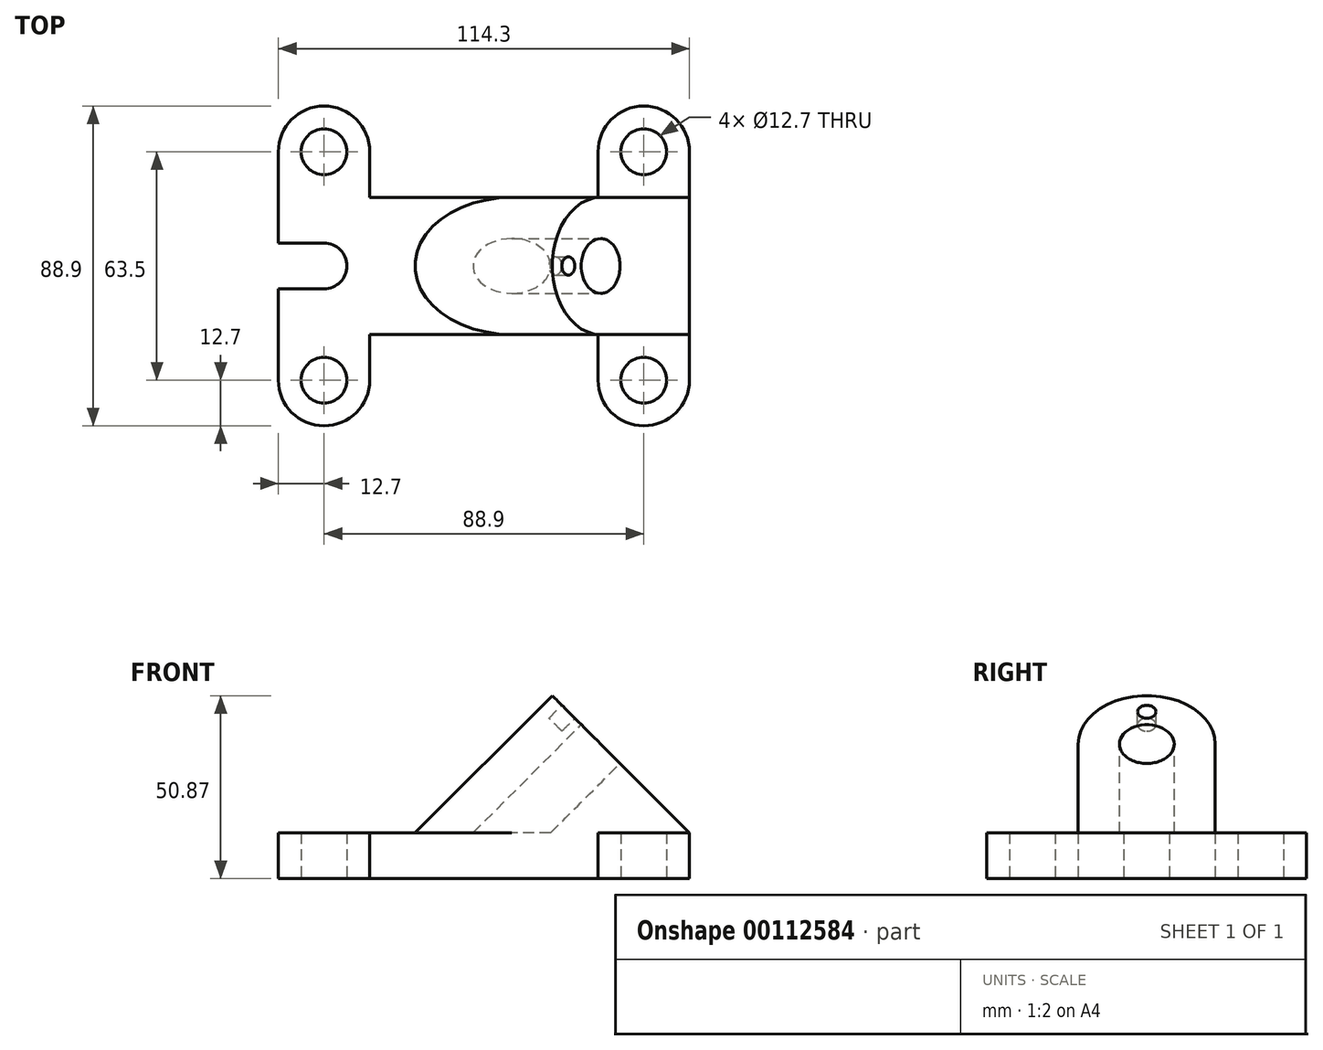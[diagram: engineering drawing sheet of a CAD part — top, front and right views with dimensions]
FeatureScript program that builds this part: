
annotation { "Feature Type Name" : "Feature", "Feature Type Description" : "" }
export const myFeature = defineFeature(function(context is Context, id is Id, definition is map)
    precondition{}
    {
        {
            var Q0;
            Q0=qCreatedBy(makeId("Top.planeOp"),FACE);
            var sketch = newSketch(context, id + "F0", { "sketchPlane" : qUnion([Q0])});
            skLineSegment(sketch, "E0", {"start": v(-14.51, 0) * mm, "end": v(127.31, 0) * mm, "construction": true});
            skLineSegment(sketch, "E1", {"start": v(0, 6.35) * mm, "end": v(0, 31.75) * mm});
            skLineSegment(sketch, "E2", {"start": v(25.4, 31.75) * mm, "end": v(25.4, 19.05) * mm});
            skLineSegment(sketch, "E3", {"start": v(25.4, 19.05) * mm, "end": v(88.9, 19.05) * mm});
            skLineSegment(sketch, "E4", {"start": v(88.9, 19.05) * mm, "end": v(88.9, 31.75) * mm});
            skLineSegment(sketch, "E5", {"start": v(114.3, 31.75) * mm, "end": v(114.3, 0) * mm});
            skArc(sketch, "E6", {"start": v(25.4, 31.75) * mm, "mid": v(12.7, 44.45) * mm, "end": v(0, 31.75) * mm});
            skArc(sketch, "E7", {"start": v(114.3, 31.75) * mm, "mid": v(101.6, 44.45) * mm, "end": v(88.9, 31.75) * mm});
            skLineSegment(sketch, "E8", {"start": v(0, 6.35) * mm, "end": v(12.7, 6.35) * mm});
            skLineSegment(sketch, "E9", {"start": v(12.7, 48.6) * mm, "end": v(12.7, -15.2) * mm, "construction": true});
            skArc(sketch, "E10", {"start": v(19.05, 0) * mm, "mid": v(17.2, 4.5) * mm, "end": v(12.7, 6.35) * mm});
            skLineSegment(sketch, "E11", {"start": v(19.05, 0) * mm, "end": v(114.3, 0) * mm});
            skCircle(sketch, "E12", {"center": v(12.7, 31.75) * mm, "radius": 6.35 * mm});
            skCircle(sketch, "E13", {"center": v(101.6, 31.75) * mm, "radius": 6.35 * mm});
            skSolve(sketch);
        }
        {
            var Q0;
            Q0=makeQuery(id+"F0.imprint","IMPRINT",FACE,{"disambiguationData":[TD([[makeQuery(id+"F0.imprint","IMPRINT",EDGE,{"derivedFrom":sQuery(id+"F0.wireOp",EDGE,"E1")}),-1.0]])]});
            extrude(context, id + "F1", {"entities" : qUnion([Q0]), "depth" : 12.7 * mm});
        }
        {
            var Q0;
            Q0=makeQuery(id+"F1.opExtrude","SWEPT_BODY",BODY,{"disambiguationData":[OSD([sQuery(id+"F0.wireOp",EDGE,"E1"),sQuery(id+"F0.wireOp",EDGE,"E2"),sQuery(id+"F0.wireOp",EDGE,"E3"),sQuery(id+"F0.wireOp",EDGE,"E4"),sQuery(id+"F0.wireOp",EDGE,"E5"),sQuery(id+"F0.wireOp",EDGE,"E6"),sQuery(id+"F0.wireOp",EDGE,"E7"),sQuery(id+"F0.wireOp",EDGE,"E8"),sQuery(id+"F0.wireOp",EDGE,"E10"),sQuery(id+"F0.wireOp",EDGE,"E11")])]});
            var Q1;
            Q1=qCreatedBy(makeId("Front.planeOp"),FACE);
            mirror(context, id + "F2", {"operationType" : NewBodyOperationType.ADD, "entities" : qUnion([Q0]), "mirrorPlane" : qUnion([Q1])});
        }
        {
            var Q0;
            {var subQ0=makeQuery(id+"F1.opExtrude","CAP_FACE",FACE,{"disambiguationData":[OSD([sQuery(id+"F0.wireOp",EDGE,"E1"),sQuery(id+"F0.wireOp",EDGE,"E2"),sQuery(id+"F0.wireOp",EDGE,"E3"),sQuery(id+"F0.wireOp",EDGE,"E4"),sQuery(id+"F0.wireOp",EDGE,"E5"),sQuery(id+"F0.wireOp",EDGE,"E6"),sQuery(id+"F0.wireOp",EDGE,"E7"),sQuery(id+"F0.wireOp",EDGE,"E8"),sQuery(id+"F0.wireOp",EDGE,"E10"),sQuery(id+"F0.wireOp",EDGE,"E11"),sQuery(id+"F0.wireOp",EDGE,"E12"),sQuery(id+"F0.wireOp",EDGE,"E13")])],"isStart":false});Q0=makeQuery(id+"F2.boolean.opBoolean","MERGE",FACE,{"derivedFrom":[subQ0,makeQuery(id+"F2.opPattern","COPY",FACE,{"derivedFrom":subQ0,"instanceName":"1"})]});}
            var Q1;
            {var subQ0=makeQuery(id+"F1.opExtrude","CAP_EDGE",EDGE,{"disambiguationData":[OSD([sQuery(id+"F0.wireOp",EDGE,"E5")])],"isStart":false});Q1=makeQuery(id+"F2.boolean.opBoolean","MERGE",EDGE,{"derivedFrom":[subQ0,makeQuery(id+"F2.opPattern","COPY",EDGE,{"derivedFrom":subQ0,"instanceName":"1"})]});}
            cPlane(context, id + "F3", {"entities" : qUnion([Q0, Q1]), "cplaneType" : CPlaneType.LINE_ANGLE, "offset" : 25.4 * mm, "angle" : 135 * degree, "width" : 152.4 * mm, "height" : 152.4 * mm});
        }
        {
            var Q0;
            Q0=qCreatedBy(id+"F3.planeOp",FACE);
            var sketch = newSketch(context, id + "F4", { "sketchPlane" : qUnion([Q0])});
            skLineSegment(sketch, "E14", {"start": v(-19.05, -71.84) * mm, "end": v(-19.05, -36.92) * mm});
            skArc(sketch, "E15", {"start": v(19.05, -36.92) * mm, "mid": v(0, -17.87) * mm, "end": v(-19.05, -36.92) * mm});
            skLineSegment(sketch, "E16", {"start": v(19.05, -36.92) * mm, "end": v(19.05, -71.84) * mm});
            skLineSegment(sketch, "E17", {"start": v(19.05, -71.84) * mm, "end": v(-19.05, -71.84) * mm});
            skCircle(sketch, "E18", {"center": v(0, -36.92) * mm, "radius": 7.62 * mm});
            skCircle(sketch, "E19", {"center": v(0, -24.22) * mm, "radius": 2.54 * mm});
            skCircle(sketch, "E20", {"center": v(0, -36.92) * mm, "radius": 12.7 * mm});
            skSolve(sketch);
        }
        {
            var Q0;
            Q0=makeQuery(id+"F4.imprint","IMPRINT",FACE,{"disambiguationData":[TD([[makeQuery(id+"F4.imprint","IMPRINT",EDGE,{"derivedFrom":sQuery(id+"F4.wireOp",EDGE,"E14")}),-1.0]])]});
            var Q1;
            Q1=makeQuery(id+"F4.imprint","IMPRINT",FACE,{"disambiguationData":[TD([[makeQuery(id+"F4.imprint","IMPRINT",EDGE,{"derivedFrom":sQuery(id+"F4.wireOp",EDGE,"E18")}),-1.0]])]});
            var Q2;
            {var subQ0=sQuery(id+"F4.wireOp",EDGE,"E20");var subQ1=sQuery(id+"F4.wireOp",EDGE,"E19");var subQ2=makeQuery(id+"F4.imprint","INTERSECT",VERTEX,{"disambiguationData":[OD(0.0)],"derivedFrom":[subQ1,subQ0]});Q2=makeQuery(id+"F4.imprint","IMPRINT",FACE,{"disambiguationData":[TD([[makeQuery(id+"F4.imprint","IMPRINT",EDGE,{"disambiguationData":[TD([[subQ2,1.0]])],"derivedFrom":subQ1}),1.0]])]});}
            var Q3;
            {var subQ0=sQuery(id+"F4.wireOp",EDGE,"E20");var subQ1=sQuery(id+"F4.wireOp",EDGE,"E19");var subQ2=makeQuery(id+"F4.imprint","INTERSECT",VERTEX,{"disambiguationData":[OD(0.0)],"derivedFrom":[subQ1,subQ0]});Q3=makeQuery(id+"F4.imprint","IMPRINT",FACE,{"disambiguationData":[TD([[makeQuery(id+"F4.imprint","IMPRINT",EDGE,{"disambiguationData":[TD([[subQ2,-1.0]])],"derivedFrom":subQ1}),1.0]])]});}
            extrude(context, id + "F5", {"entities" : qUnion([Q0, Q1, Q2, Q3]), "operationType" : NewBodyOperationType.ADD, "endBound" : BoundingType.UP_TO_NEXT, "oppositeDirection" : true, "depth" : 6.35 * mm});
        }
        {
            var Q0;
            {var subQ0=sQuery(id+"F4.wireOp",EDGE,"E20");var subQ1=sQuery(id+"F4.wireOp",EDGE,"E19");var subQ2=makeQuery(id+"F4.imprint","INTERSECT",VERTEX,{"disambiguationData":[OD(0.0)],"derivedFrom":[subQ1,subQ0]});Q0=makeQuery(id+"F4.imprint","IMPRINT",FACE,{"disambiguationData":[TD([[makeQuery(id+"F4.imprint","IMPRINT",EDGE,{"disambiguationData":[TD([[subQ2,1.0]])],"derivedFrom":subQ1}),1.0]])]});}
            var Q1;
            {var subQ0=sQuery(id+"F4.wireOp",EDGE,"E20");var subQ1=sQuery(id+"F4.wireOp",EDGE,"E19");var subQ2=makeQuery(id+"F4.imprint","INTERSECT",VERTEX,{"disambiguationData":[OD(0.0)],"derivedFrom":[subQ1,subQ0]});Q1=makeQuery(id+"F4.imprint","IMPRINT",FACE,{"disambiguationData":[TD([[makeQuery(id+"F4.imprint","IMPRINT",EDGE,{"disambiguationData":[TD([[subQ2,-1.0]])],"derivedFrom":subQ1}),1.0]])]});}
            extrude(context, id + "F6", {"entities" : qUnion([Q0, Q1]), "operationType" : NewBodyOperationType.REMOVE, "oppositeDirection" : true, "depth" : 5.08 * mm});
        }
    });
